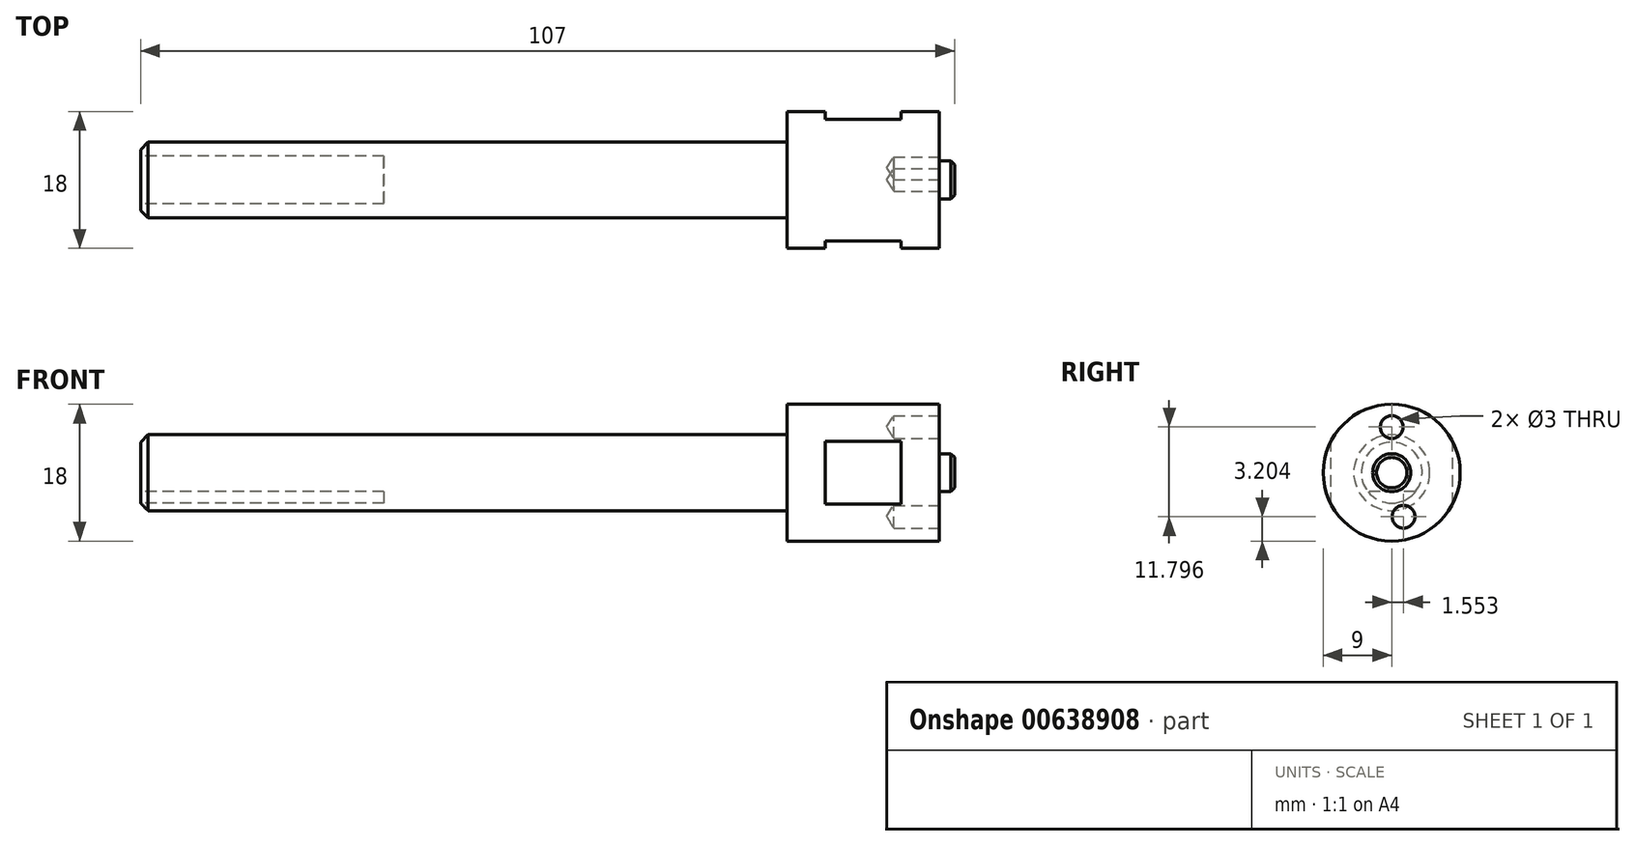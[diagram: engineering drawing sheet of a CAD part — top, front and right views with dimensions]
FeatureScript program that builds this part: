
annotation { "Feature Type Name" : "Feature", "Feature Type Description" : "" }
export const myFeature = defineFeature(function(context is Context, id is Id, definition is map)
    precondition{}
    {
        {
            var Q0;
            Q0=qCreatedBy(makeId("Front.planeOp"),FACE);
            var sketch = newSketch(context, id + "F0", { "sketchPlane" : qUnion([Q0])});
            skCircle(sketch, "E0", {"center": v(-171.85, -5.8) * mm, "radius": 1.23 * mm});
            skArc(sketch, "E1", {"start": v(-171.46, -4.35) * mm, "mid": v(-173.15, -6.55) * mm, "end": v(-170.4, -6.18) * mm});
            skCircle(sketch, "E2", {"center": v(-170.3, 6) * mm, "radius": 1.23 * mm});
            skArc(sketch, "E3", {"start": v(-169.9, 7.45) * mm, "mid": v(-171.6, 5.25) * mm, "end": v(-168.85, 5.61) * mm});
            skLineSegment(sketch, "E4", {"start": v(-162.3, -4.12) * mm, "end": v(-162.3, 4.12) * mm});
            skLineSegment(sketch, "E5", {"start": v(-178.3, -4.12) * mm, "end": v(-178.3, 4.12) * mm});
            skCircle(sketch, "E6", {"center": v(-170.3, 0) * mm, "radius": 9 * mm});
            skLineSegment(sketch, "E7", {"start": v(-174.63, -2.5) * mm, "end": v(-165.97, -2.5) * mm});
            skArc(sketch, "E8", {"start": v(-167.17, -2.5) * mm, "mid": v(-170.3, 4) * mm, "end": v(-173.42, -2.5) * mm});
            skCircle(sketch, "E9", {"center": v(-170.3, 0) * mm, "radius": 2.5 * mm});
            skCircle(sketch, "E10", {"center": v(-170.3, 0) * mm, "radius": 5 * mm});
            skLineSegment(sketch, "E11", {"start": v(1.5, 2.5) * mm, "end": v(1.5, -2.5) * mm});
            skLineSegment(sketch, "E12", {"start": v(2, 0) * mm, "end": v(-108, 0) * mm});
            skLineSegment(sketch, "E13", {"start": v(-104, 5) * mm, "end": v(-20, 5) * mm});
            skLineSegment(sketch, "E14", {"start": v(-73, -5) * mm, "end": v(-20, -5) * mm});
            skLineSegment(sketch, "E15", {"start": v(-105, 4) * mm, "end": v(-104, 5) * mm});
            skLineSegment(sketch, "E16", {"start": v(-105, 4) * mm, "end": v(-105, -2.5) * mm});
            skLineSegment(sketch, "E17", {"start": v(-104, -2.5) * mm, "end": v(-104, 5) * mm});
            skLineSegment(sketch, "E18", {"start": v(-73, -2.5) * mm, "end": v(-73, -5) * mm});
            skLineSegment(sketch, "E19", {"start": v(-105, -2.5) * mm, "end": v(-73, -2.5) * mm});
            skLineSegment(sketch, "E20", {"start": v(2, 2) * mm, "end": v(1.5, 2.5) * mm});
            skLineSegment(sketch, "E21", {"start": v(1.5, -2.5) * mm, "end": v(2, -2) * mm});
            skLineSegment(sketch, "E22", {"start": v(0, 9) * mm, "end": v(0, -9) * mm});
            skLineSegment(sketch, "E23", {"start": v(-9.03, -6) * mm, "end": v(0.82, -6) * mm});
            skLineSegment(sketch, "E24", {"start": v(-6, -7.5) * mm, "end": v(-6.47, -7.23) * mm});
            skLineSegment(sketch, "E25", {"start": v(-6, -4.5) * mm, "end": v(-6.47, -4.77) * mm});
            skLineSegment(sketch, "E26", {"start": v(0, -7.5) * mm, "end": v(-6, -7.5) * mm});
            skLineSegment(sketch, "E27", {"start": v(-6, -4.5) * mm, "end": v(0, -4.5) * mm});
            skLineSegment(sketch, "E28", {"start": v(-6, -7.5) * mm, "end": v(-6, -4.5) * mm});
            skLineSegment(sketch, "E29", {"start": v(-7.5, -7.23) * mm, "end": v(-8.21, -6) * mm});
            skLineSegment(sketch, "E30", {"start": v(-7.5, -4.77) * mm, "end": v(-8.21, -6) * mm});
            skLineSegment(sketch, "E31", {"start": v(-7.5, -4.77) * mm, "end": v(0, -4.77) * mm});
            skLineSegment(sketch, "E32", {"start": v(-7.5, -7.23) * mm, "end": v(-7.5, -4.77) * mm});
            skLineSegment(sketch, "E33", {"start": v(0, -7.23) * mm, "end": v(-7.5, -7.23) * mm});
            skLineSegment(sketch, "E34", {"start": v(-9.03, 6) * mm, "end": v(0.82, 6) * mm});
            skLineSegment(sketch, "E35", {"start": v(-6, 7.5) * mm, "end": v(-6.47, 7.23) * mm});
            skLineSegment(sketch, "E36", {"start": v(-6, 4.5) * mm, "end": v(-6.47, 4.77) * mm});
            skLineSegment(sketch, "E37", {"start": v(0, 7.5) * mm, "end": v(-6, 7.5) * mm});
            skLineSegment(sketch, "E38", {"start": v(-6, 4.5) * mm, "end": v(0, 4.5) * mm});
            skLineSegment(sketch, "E39", {"start": v(-6, 7.5) * mm, "end": v(-6, 4.5) * mm});
            skLineSegment(sketch, "E40", {"start": v(-7.5, 7.23) * mm, "end": v(-8.21, 6) * mm});
            skLineSegment(sketch, "E41", {"start": v(-7.5, 4.77) * mm, "end": v(-8.21, 6) * mm});
            skLineSegment(sketch, "E42", {"start": v(-7.5, 4.77) * mm, "end": v(0, 4.77) * mm});
            skLineSegment(sketch, "E43", {"start": v(-7.5, 7.23) * mm, "end": v(-7.5, 4.77) * mm});
            skLineSegment(sketch, "E44", {"start": v(0, 7.23) * mm, "end": v(-7.5, 7.23) * mm});
            skLineSegment(sketch, "E45", {"start": v(2, 2) * mm, "end": v(2, -2) * mm});
            skLineSegment(sketch, "E46", {"start": v(1.5, 2.5) * mm, "end": v(0, 2.5) * mm});
            skLineSegment(sketch, "E47", {"start": v(-5, -4.12) * mm, "end": v(-15, 4.12) * mm});
            skLineSegment(sketch, "E48", {"start": v(-15, -4.12) * mm, "end": v(-5, 4.12) * mm});
            skLineSegment(sketch, "E49", {"start": v(-5, 4.12) * mm, "end": v(-5, -4.12) * mm});
            skLineSegment(sketch, "E50", {"start": v(-15, 4.12) * mm, "end": v(-15, -4.12) * mm});
            skLineSegment(sketch, "E51", {"start": v(0, -9) * mm, "end": v(-20, -9) * mm});
            skLineSegment(sketch, "E52", {"start": v(-20, 9) * mm, "end": v(-20, -9) * mm});
            skLineSegment(sketch, "E53", {"start": v(0, 9) * mm, "end": v(-20, 9) * mm});
            skLineSegment(sketch, "E54", {"start": v(-5, -4.12) * mm, "end": v(-15, -4.12) * mm});
            skLineSegment(sketch, "E55", {"start": v(-5, 4.12) * mm, "end": v(-15, 4.12) * mm});
            skLineSegment(sketch, "E56", {"start": v(1.5, -2.5) * mm, "end": v(0, -2.5) * mm});
            skLineSegment(sketch, "E57", {"start": v(1.5, 33.8) * mm, "end": v(1.5, 28.8) * mm});
            skLineSegment(sketch, "E58", {"start": v(2, 31.3) * mm, "end": v(-108, 31.3) * mm});
            skLineSegment(sketch, "E59", {"start": v(-104, 36.3) * mm, "end": v(-20, 36.3) * mm});
            skLineSegment(sketch, "E60", {"start": v(-104, 26.3) * mm, "end": v(-20, 26.3) * mm});
            skLineSegment(sketch, "E61", {"start": v(-105, 35.3) * mm, "end": v(-104, 36.3) * mm});
            skLineSegment(sketch, "E62", {"start": v(-105, 35.3) * mm, "end": v(-105, 28.8) * mm});
            skLineSegment(sketch, "E63", {"start": v(-104, 28.8) * mm, "end": v(-104, 36.3) * mm});
            skLineSegment(sketch, "E64", {"start": v(2, 33.3) * mm, "end": v(1.5, 33.8) * mm});
            skLineSegment(sketch, "E65", {"start": v(1.5, 28.8) * mm, "end": v(2, 29.3) * mm});
            skLineSegment(sketch, "E66", {"start": v(0, 40.3) * mm, "end": v(0, 22.3) * mm});
            skLineSegment(sketch, "E67", {"start": v(-9.03, 25.3) * mm, "end": v(0.82, 25.3) * mm});
            skLineSegment(sketch, "E68", {"start": v(-6, 23.8) * mm, "end": v(-6.47, 24.07) * mm});
            skLineSegment(sketch, "E69", {"start": v(-6, 26.8) * mm, "end": v(-6.47, 26.53) * mm});
            skLineSegment(sketch, "E70", {"start": v(0, 23.8) * mm, "end": v(-6, 23.8) * mm});
            skLineSegment(sketch, "E71", {"start": v(-6, 26.8) * mm, "end": v(0, 26.8) * mm});
            skLineSegment(sketch, "E72", {"start": v(-6, 23.8) * mm, "end": v(-6, 26.8) * mm});
            skLineSegment(sketch, "E73", {"start": v(-7.5, 24.07) * mm, "end": v(-8.21, 25.3) * mm});
            skLineSegment(sketch, "E74", {"start": v(-7.5, 26.53) * mm, "end": v(-8.21, 25.3) * mm});
            skLineSegment(sketch, "E75", {"start": v(-7.5, 26.53) * mm, "end": v(0, 26.53) * mm});
            skLineSegment(sketch, "E76", {"start": v(-7.5, 24.07) * mm, "end": v(-7.5, 26.53) * mm});
            skLineSegment(sketch, "E77", {"start": v(0, 24.07) * mm, "end": v(-7.5, 24.07) * mm});
            skLineSegment(sketch, "E78", {"start": v(-9.03, 37.3) * mm, "end": v(0.82, 37.3) * mm});
            skLineSegment(sketch, "E79", {"start": v(-6, 38.8) * mm, "end": v(-6.47, 38.53) * mm});
            skLineSegment(sketch, "E80", {"start": v(-6, 35.8) * mm, "end": v(-6.47, 36.07) * mm});
            skLineSegment(sketch, "E81", {"start": v(0, 38.8) * mm, "end": v(-6, 38.8) * mm});
            skLineSegment(sketch, "E82", {"start": v(-6, 35.8) * mm, "end": v(0, 35.8) * mm});
            skLineSegment(sketch, "E83", {"start": v(-6, 38.8) * mm, "end": v(-6, 35.8) * mm});
            skLineSegment(sketch, "E84", {"start": v(-7.5, 38.53) * mm, "end": v(-8.21, 37.3) * mm});
            skLineSegment(sketch, "E85", {"start": v(-7.5, 36.07) * mm, "end": v(-8.21, 37.3) * mm});
            skLineSegment(sketch, "E86", {"start": v(-7.5, 36.07) * mm, "end": v(0, 36.07) * mm});
            skLineSegment(sketch, "E87", {"start": v(-7.5, 38.53) * mm, "end": v(-7.5, 36.07) * mm});
            skLineSegment(sketch, "E88", {"start": v(0, 38.53) * mm, "end": v(-7.5, 38.53) * mm});
            skLineSegment(sketch, "E89", {"start": v(2, 33.3) * mm, "end": v(2, 29.3) * mm});
            skLineSegment(sketch, "E90", {"start": v(1.5, 33.8) * mm, "end": v(0, 33.8) * mm});
            skLineSegment(sketch, "E91", {"start": v(0, 22.3) * mm, "end": v(-5, 22.3) * mm});
            skLineSegment(sketch, "E92", {"start": v(-20, 40.3) * mm, "end": v(-20, 22.3) * mm});
            skLineSegment(sketch, "E93", {"start": v(0, 40.3) * mm, "end": v(-5, 40.3) * mm});
            skLineSegment(sketch, "E94", {"start": v(1.5, 28.8) * mm, "end": v(0, 28.8) * mm});
            skLineSegment(sketch, "E95", {"start": v(-105, 27.3) * mm, "end": v(-104, 26.3) * mm});
            skLineSegment(sketch, "E96", {"start": v(-105, 27.3) * mm, "end": v(-105, 33.8) * mm});
            skLineSegment(sketch, "E97", {"start": v(-104, 33.8) * mm, "end": v(-104, 26.3) * mm});
            skLineSegment(sketch, "E98", {"start": v(-5, 40.3) * mm, "end": v(-5, 39.3) * mm});
            skLineSegment(sketch, "E99", {"start": v(-15, 40.3) * mm, "end": v(-15, 39.3) * mm});
            skLineSegment(sketch, "E100", {"start": v(-5, 39.3) * mm, "end": v(-15, 39.3) * mm});
            skLineSegment(sketch, "E101", {"start": v(-5, 23.3) * mm, "end": v(-15, 23.3) * mm});
            skLineSegment(sketch, "E102", {"start": v(-5, 23.3) * mm, "end": v(-5, 22.3) * mm});
            skLineSegment(sketch, "E103", {"start": v(-15, 23.3) * mm, "end": v(-15, 22.3) * mm});
            skLineSegment(sketch, "E104", {"start": v(-15, 22.3) * mm, "end": v(-20, 22.3) * mm});
            skLineSegment(sketch, "E105", {"start": v(-15, 40.3) * mm, "end": v(-20, 40.3) * mm});
            skLineSegment(sketch, "E106", {"start": v(-73, 36.3) * mm, "end": v(-73, 26.3) * mm});
            skSolve(sketch);
        }
        {
            var Q0;
            {var subQ0=sQuery(id+"F0.wireOp",EDGE,"E46");Q0=makeQuery(id+"F0.imprint","IMPRINT",FACE,{"disambiguationData":[TD([[makeQuery(id+"F0.imprint","IMPRINT",EDGE,{"derivedFrom":subQ0}),1.0]])]});}
            var Q1;
            {var subQ0=sQuery(id+"F0.wireOp",EDGE,"E49");var subQ1=sQuery(id+"F0.wireOp",EDGE,"E12");var subQ2=makeQuery(id+"F0.imprint","INTERSECT",VERTEX,{"derivedFrom":[subQ1,subQ0]});Q1=makeQuery(id+"F0.imprint","IMPRINT",FACE,{"disambiguationData":[TD([[makeQuery(id+"F0.imprint","IMPRINT",EDGE,{"disambiguationData":[TD([[subQ2,-1.0]])],"derivedFrom":subQ1}),-1.0]])]});}
            var Q2;
            {var subQ0=sQuery(id+"F0.wireOp",EDGE,"E40");Q2=makeQuery(id+"F0.imprint","IMPRINT",FACE,{"disambiguationData":[TD([[makeQuery(id+"F0.imprint","IMPRINT",EDGE,{"derivedFrom":subQ0}),1.0]])]});}
            var Q3;
            {var subQ0=sQuery(id+"F0.wireOp",EDGE,"E50");var subQ1=sQuery(id+"F0.wireOp",EDGE,"E12");var subQ2=makeQuery(id+"F0.imprint","INTERSECT",VERTEX,{"derivedFrom":[subQ1,subQ0]});Q3=makeQuery(id+"F0.imprint","IMPRINT",FACE,{"disambiguationData":[TD([[makeQuery(id+"F0.imprint","IMPRINT",EDGE,{"disambiguationData":[TD([[subQ2,1.0]])],"derivedFrom":subQ1}),-1.0]])]});}
            var Q4;
            {var subQ5=sQuery(id+"F0.wireOp",EDGE,"E13");Q4=makeQuery(id+"F0.imprint","IMPRINT",FACE,{"disambiguationData":[TD([[makeQuery(id+"F0.imprint","IMPRINT",EDGE,{"derivedFrom":subQ5}),-1.0]])]});}
            var Q5;
            {var subQ17=sQuery(id+"F0.wireOp",EDGE,"E35");Q5=makeQuery(id+"F0.imprint","IMPRINT",FACE,{"disambiguationData":[TD([[makeQuery(id+"F0.imprint","IMPRINT",EDGE,{"derivedFrom":subQ17}),-1.0]])]});}
            var Q6;
            {var subQ0=sQuery(id+"F0.wireOp",EDGE,"E55");Q6=makeQuery(id+"F0.imprint","IMPRINT",FACE,{"disambiguationData":[TD([[makeQuery(id+"F0.imprint","IMPRINT",EDGE,{"derivedFrom":subQ0}),1.0]])]});}
            var Q7;
            {var subQ0=sQuery(id+"F0.wireOp",EDGE,"E44");var subQ1=sQuery(id+"F0.wireOp",EDGE,"E22");var subQ2=makeQuery(id+"F0.imprint","INTERSECT",VERTEX,{"derivedFrom":[subQ1,subQ0]});Q7=makeQuery(id+"F0.imprint","IMPRINT",FACE,{"disambiguationData":[TD([[makeQuery(id+"F0.imprint","IMPRINT",EDGE,{"disambiguationData":[TD([[subQ2,-1.0]])],"derivedFrom":subQ1}),-1.0]])]});}
            var Q8;
            {var subQ0=sQuery(id+"F0.wireOp",EDGE,"E20");Q8=makeQuery(id+"F0.imprint","IMPRINT",FACE,{"disambiguationData":[TD([[makeQuery(id+"F0.imprint","IMPRINT",EDGE,{"derivedFrom":subQ0}),1.0]])]});}
            var Q9;
            {var subQ0=sQuery(id+"F0.wireOp",EDGE,"E42");var subQ1=sQuery(id+"F0.wireOp",EDGE,"E22");var subQ2=makeQuery(id+"F0.imprint","INTERSECT",VERTEX,{"derivedFrom":[subQ1,subQ0]});Q9=makeQuery(id+"F0.imprint","IMPRINT",FACE,{"disambiguationData":[TD([[makeQuery(id+"F0.imprint","IMPRINT",EDGE,{"disambiguationData":[TD([[subQ2,1.0]])],"derivedFrom":subQ1}),-1.0]])]});}
            var Q10;
            {var subQ4=sQuery(id+"F0.wireOp",EDGE,"E34");var subQ6=sQuery(id+"F0.wireOp",EDGE,"E43");var subQ8=makeQuery(id+"F0.imprint","INTERSECT",VERTEX,{"derivedFrom":[subQ4,subQ6]});Q10=makeQuery(id+"F0.imprint","IMPRINT",FACE,{"disambiguationData":[TD([[makeQuery(id+"F0.imprint","IMPRINT",EDGE,{"disambiguationData":[TD([[subQ8,-1.0]])],"derivedFrom":subQ4}),1.0]])]});}
            var Q11;
            {var subQ2=sQuery(id+"F0.wireOp",EDGE,"E43");var subQ6=sQuery(id+"F0.wireOp",EDGE,"E34");var subQ8=makeQuery(id+"F0.imprint","INTERSECT",VERTEX,{"derivedFrom":[subQ6,subQ2]});Q11=makeQuery(id+"F0.imprint","IMPRINT",FACE,{"disambiguationData":[TD([[makeQuery(id+"F0.imprint","IMPRINT",EDGE,{"disambiguationData":[TD([[subQ8,-1.0]])],"derivedFrom":subQ6}),-1.0]])]});}
            var Q12;
            {var subQ0=sQuery(id+"F0.wireOp",EDGE,"E41");Q12=makeQuery(id+"F0.imprint","IMPRINT",FACE,{"disambiguationData":[TD([[makeQuery(id+"F0.imprint","IMPRINT",EDGE,{"derivedFrom":subQ0}),-1.0]])]});}
            var Q13;
            {var subQ0=sQuery(id+"F0.wireOp",EDGE,"E37");Q13=makeQuery(id+"F0.imprint","IMPRINT",FACE,{"disambiguationData":[TD([[makeQuery(id+"F0.imprint","IMPRINT",EDGE,{"derivedFrom":subQ0}),1.0]])]});}
            var Q14;
            {var subQ0=sQuery(id+"F0.wireOp",EDGE,"E38");Q14=makeQuery(id+"F0.imprint","IMPRINT",FACE,{"disambiguationData":[TD([[makeQuery(id+"F0.imprint","IMPRINT",EDGE,{"derivedFrom":subQ0}),1.0]])]});}
            var Q15;
            {var subQ0=sQuery(id+"F0.wireOp",EDGE,"E36");Q15=makeQuery(id+"F0.imprint","IMPRINT",FACE,{"disambiguationData":[TD([[makeQuery(id+"F0.imprint","IMPRINT",EDGE,{"derivedFrom":subQ0}),-1.0]])]});}
            var Q16;
            {var subQ0=sQuery(id+"F0.wireOp",EDGE,"E35");Q16=makeQuery(id+"F0.imprint","IMPRINT",FACE,{"disambiguationData":[TD([[makeQuery(id+"F0.imprint","IMPRINT",EDGE,{"derivedFrom":subQ0}),1.0]])]});}
            var Q17;
            {var subQ5=sQuery(id+"F0.wireOp",EDGE,"E15");Q17=makeQuery(id+"F0.imprint","IMPRINT",FACE,{"disambiguationData":[TD([[makeQuery(id+"F0.imprint","IMPRINT",EDGE,{"derivedFrom":subQ5}),-1.0]])]});}
            var Q18;
            Q18=sQuery(id+"F0.wireOp",EDGE,"E12");
            revolve(context, id + "F1", {"entities" : qUnion([Q0, Q1, Q2, Q3, Q4, Q5, Q6, Q7, Q8, Q9, Q10, Q11, Q12, Q13, Q14, Q15, Q16, Q17]), "axis" : qUnion([Q18]), "revolveType" : RevolveType.FULL});
        }
        {
            var Q0;
            Q0=makeQuery(id+"F1.opRevolve","SWEPT_FACE",FACE,{"disambiguationData":[OSD([sQuery(id+"F0.wireOp",EDGE,"E16")])]});
            var sketch = newSketch(context, id + "F2", { "sketchPlane" : qUnion([Q0])});
            skCircle(sketch, "E107.0", {"center": v(0, 0) * mm, "radius": 5 * mm});
            skLineSegment(sketch, "E108.0", {"start": v(-4.33, -2.5) * mm, "end": v(4.33, -2.5) * mm});
            skCircle(sketch, "E109.0", {"center": v(0, 0) * mm, "radius": 4 * mm});
            skSolve(sketch);
        }
        {
            var Q0;
            {var subQ0=sQuery(id+"F2.wireOp",EDGE,"E108.0");var subQ1=makeQuery(id+"F1.opRevolve","SWEPT_EDGE",EDGE,{"disambiguationData":[OSD([sQuery(id+"F0.wireOp",EDGE,"E15"),sQuery(id+"F0.wireOp",EDGE,"E16")])]});var subQ2=makeQuery(id+"F2.imprint","INTERSECT",VERTEX,{"disambiguationData":[OD(0.0)],"derivedFrom":[subQ1,subQ0]});Q0=makeQuery(id+"F2.imprint","IMPRINT",FACE,{"disambiguationData":[TD([[makeQuery(id+"F2.imprint","IMPRINT",EDGE,{"disambiguationData":[TD([[subQ2,-1.0]])],"derivedFrom":subQ0}),-1.0]])]});}
            var Q1;
            {var subQ0=sQuery(id+"F2.wireOp",EDGE,"E108.0");var subQ1=sQuery(id+"F2.wireOp",EDGE,"E107.0");var subQ2=makeQuery(id+"F2.imprint","INTERSECT",VERTEX,{"disambiguationData":[OD(0.0)],"derivedFrom":[subQ1,subQ0]});Q1=makeQuery(id+"F2.imprint","IMPRINT",FACE,{"disambiguationData":[TD([[makeQuery(id+"F2.imprint","IMPRINT",EDGE,{"disambiguationData":[TD([[subQ2,1.0]])],"derivedFrom":subQ1}),-1.0]])]});}
            var Q2;
            {var subQ0=sQuery(id+"F2.wireOp",EDGE,"E109.0");var subQ1=sQuery(id+"F2.wireOp",EDGE,"E108.0");var subQ2=makeQuery(id+"F2.imprint","INTERSECT",VERTEX,{"disambiguationData":[OD(0.0)],"derivedFrom":[subQ1,subQ0]});Q2=makeQuery(id+"F2.imprint","IMPRINT",FACE,{"disambiguationData":[TD([[makeQuery(id+"F2.imprint","IMPRINT",EDGE,{"disambiguationData":[TD([[subQ2,-1.0]])],"derivedFrom":subQ1}),-1.0]])]});}
            extrude(context, id + "F3", {"entities" : qUnion([Q0, Q1, Q2]), "operationType" : NewBodyOperationType.REMOVE, "oppositeDirection" : true, "depth" : 32 * mm, "offsetDistance" : 25 * mm});
        }
        {
            var Q0;
            Q0=qCreatedBy(makeId("Top.planeOp"),FACE);
            var sketch = newSketch(context, id + "F4", { "sketchPlane" : qUnion([Q0])});
            skLineSegment(sketch, "E110", {"start": v(1.5, 2.5) * mm, "end": v(1.5, -2.5) * mm});
            skLineSegment(sketch, "E111", {"start": v(2, 0) * mm, "end": v(-108, 0) * mm});
            skLineSegment(sketch, "E112", {"start": v(-104, 5) * mm, "end": v(-20, 5) * mm});
            skLineSegment(sketch, "E113", {"start": v(-104, -5) * mm, "end": v(-20, -5) * mm});
            skLineSegment(sketch, "E114", {"start": v(-105, 4) * mm, "end": v(-104, 5) * mm});
            skLineSegment(sketch, "E115", {"start": v(-105, 4) * mm, "end": v(-105, -2.5) * mm});
            skLineSegment(sketch, "E116", {"start": v(-104, -2.5) * mm, "end": v(-104, 5) * mm});
            skLineSegment(sketch, "E117", {"start": v(2, 2) * mm, "end": v(1.5, 2.5) * mm});
            skLineSegment(sketch, "E118", {"start": v(1.5, -2.5) * mm, "end": v(2, -2) * mm});
            skLineSegment(sketch, "E119", {"start": v(0, 9) * mm, "end": v(0, -9) * mm});
            skLineSegment(sketch, "E120", {"start": v(-9.03, -6) * mm, "end": v(0.82, -6) * mm});
            skLineSegment(sketch, "E121", {"start": v(-6, -7.5) * mm, "end": v(-6.47, -7.23) * mm});
            skLineSegment(sketch, "E122", {"start": v(-6, -4.5) * mm, "end": v(-6.47, -4.77) * mm});
            skLineSegment(sketch, "E123", {"start": v(0, -7.5) * mm, "end": v(-6, -7.5) * mm});
            skLineSegment(sketch, "E124", {"start": v(-6, -4.5) * mm, "end": v(0, -4.5) * mm});
            skLineSegment(sketch, "E125", {"start": v(-6, -7.5) * mm, "end": v(-6, -4.5) * mm});
            skLineSegment(sketch, "E126", {"start": v(-7.5, -7.23) * mm, "end": v(-8.21, -6) * mm});
            skLineSegment(sketch, "E127", {"start": v(-7.5, -4.77) * mm, "end": v(-8.21, -6) * mm});
            skLineSegment(sketch, "E128", {"start": v(-7.5, -4.77) * mm, "end": v(0, -4.77) * mm});
            skLineSegment(sketch, "E129", {"start": v(-7.5, -7.23) * mm, "end": v(-7.5, -4.77) * mm});
            skLineSegment(sketch, "E130", {"start": v(0, -7.23) * mm, "end": v(-7.5, -7.23) * mm});
            skLineSegment(sketch, "E131", {"start": v(-9.03, 6) * mm, "end": v(0.82, 6) * mm});
            skLineSegment(sketch, "E132", {"start": v(-6, 7.5) * mm, "end": v(-6.47, 7.23) * mm});
            skLineSegment(sketch, "E133", {"start": v(-6, 4.5) * mm, "end": v(-6.47, 4.77) * mm});
            skLineSegment(sketch, "E134", {"start": v(0, 7.5) * mm, "end": v(-6, 7.5) * mm});
            skLineSegment(sketch, "E135", {"start": v(-6, 4.5) * mm, "end": v(0, 4.5) * mm});
            skLineSegment(sketch, "E136", {"start": v(-6, 7.5) * mm, "end": v(-6, 4.5) * mm});
            skLineSegment(sketch, "E137", {"start": v(-7.5, 7.23) * mm, "end": v(-8.21, 6) * mm});
            skLineSegment(sketch, "E138", {"start": v(-7.5, 4.77) * mm, "end": v(-8.21, 6) * mm});
            skLineSegment(sketch, "E139", {"start": v(-7.5, 4.77) * mm, "end": v(0, 4.77) * mm});
            skLineSegment(sketch, "E140", {"start": v(-7.5, 7.23) * mm, "end": v(-7.5, 4.77) * mm});
            skLineSegment(sketch, "E141", {"start": v(0, 7.23) * mm, "end": v(-7.5, 7.23) * mm});
            skLineSegment(sketch, "E142", {"start": v(2, 2) * mm, "end": v(2, -2) * mm});
            skLineSegment(sketch, "E143", {"start": v(1.5, 2.5) * mm, "end": v(0, 2.5) * mm});
            skLineSegment(sketch, "E144", {"start": v(0, -9) * mm, "end": v(-5, -9) * mm});
            skLineSegment(sketch, "E145", {"start": v(-20, 9) * mm, "end": v(-20, -9) * mm});
            skLineSegment(sketch, "E146", {"start": v(0, 9) * mm, "end": v(-5, 9) * mm});
            skLineSegment(sketch, "E147", {"start": v(1.5, -2.5) * mm, "end": v(0, -2.5) * mm});
            skLineSegment(sketch, "E148", {"start": v(-105, -4) * mm, "end": v(-104, -5) * mm});
            skLineSegment(sketch, "E149", {"start": v(-105, -4) * mm, "end": v(-105, 2.5) * mm});
            skLineSegment(sketch, "E150", {"start": v(-104, 2.5) * mm, "end": v(-104, -5) * mm});
            skLineSegment(sketch, "E151", {"start": v(-5, 9) * mm, "end": v(-5, 8) * mm});
            skLineSegment(sketch, "E152", {"start": v(-15, 9) * mm, "end": v(-15, 8) * mm});
            skLineSegment(sketch, "E153", {"start": v(-5, 8) * mm, "end": v(-15, 8) * mm});
            skLineSegment(sketch, "E154", {"start": v(-5, -8) * mm, "end": v(-15, -8) * mm});
            skLineSegment(sketch, "E155", {"start": v(-5, -8) * mm, "end": v(-5, -9) * mm});
            skLineSegment(sketch, "E156", {"start": v(-15, -8) * mm, "end": v(-15, -9) * mm});
            skLineSegment(sketch, "E157", {"start": v(-15, -9) * mm, "end": v(-20, -9) * mm});
            skLineSegment(sketch, "E158", {"start": v(-15, 9) * mm, "end": v(-20, 9) * mm});
            skLineSegment(sketch, "E159", {"start": v(-73, 5) * mm, "end": v(-73, -5) * mm});
            skLineSegment(sketch, "E160", {"start": v(-20, 9) * mm, "end": v(0, 9) * mm});
            skLineSegment(sketch, "E161", {"start": v(0, -9) * mm, "end": v(-20, -9) * mm});
            skSolve(sketch);
        }
        {
            var Q0;
            Q0=makeQuery(id+"F4.imprint","IMPRINT",FACE,{"disambiguationData":[TD([[makeQuery(id+"F4.imprint","IMPRINT",EDGE,{"derivedFrom":sQuery(id+"F4.wireOp",EDGE,"E154")}),1.0]])]});
            var Q1;
            {var subQ0=sQuery(id+"F4.wireOp",EDGE,"E151");Q1=makeQuery(id+"F4.imprint","IMPRINT",FACE,{"disambiguationData":[TD([[makeQuery(id+"F4.imprint","IMPRINT",EDGE,{"derivedFrom":subQ0}),-1.0]])]});}
            extrude(context, id + "F5", {"entities" : qUnion([Q0, Q1]), "operationType" : NewBodyOperationType.REMOVE, "endBound" : BoundingType.SYMMETRIC, "oppositeDirection" : true, "depth" : 25 * mm, "offsetDistance" : 25 * mm});
        }
        {
            var Q0;
            Q0=makeQuery(id+"F1.opRevolve","SWEPT_FACE",FACE,{"disambiguationData":[OSD([sQuery(id+"F0.wireOp",EDGE,"E52")])]});
            var sketch = newSketch(context, id + "F6", { "sketchPlane" : qUnion([Q0])});
            skCircle(sketch, "E162", {"center": v(-1.55, -5.8) * mm, "radius": 1.23 * mm});
            skArc(sketch, "E163", {"start": v(-1.16, -4.35) * mm, "mid": v(-2.85, -6.55) * mm, "end": v(-0.1, -6.18) * mm});
            skCircle(sketch, "E164", {"center": v(0, 6) * mm, "radius": 1.23 * mm});
            skArc(sketch, "E165", {"start": v(0.39, 7.45) * mm, "mid": v(-1.3, 5.25) * mm, "end": v(1.45, 5.61) * mm});
            skLineSegment(sketch, "E166", {"start": v(8, -4.12) * mm, "end": v(8, 4.12) * mm});
            skLineSegment(sketch, "E167", {"start": v(-8, -4.12) * mm, "end": v(-8, 4.12) * mm});
            skCircle(sketch, "E168", {"center": v(0, 0) * mm, "radius": 9 * mm});
            skLineSegment(sketch, "E169", {"start": v(-4.33, -2.5) * mm, "end": v(4.33, -2.5) * mm});
            skArc(sketch, "E170", {"start": v(3.12, -2.5) * mm, "mid": v(0, 4) * mm, "end": v(-3.12, -2.5) * mm});
            skCircle(sketch, "E171", {"center": v(0, 0) * mm, "radius": 2.5 * mm});
            skCircle(sketch, "E172", {"center": v(0, 0) * mm, "radius": 5 * mm});
            skSolve(sketch);
        }
        {
            var Q0;
            Q0=makeQuery(id+"F1.opRevolve","SWEPT_FACE",FACE,{"disambiguationData":[OSD([sQuery(id+"F0.wireOp",EDGE,"E22")])]});
            var sketch = newSketch(context, id + "F7", { "sketchPlane" : qUnion([Q0])});
            skPoint(sketch, "E173.0", {"position": v(0, 6) * mm});
            skPoint(sketch, "E174.0", {"position": v(1.55, -5.8) * mm});
            skSolve(sketch);
        }
        {
            var Q0;
            Q0=sQuery(id+"F7.wireOp",VERTEX,"E173.0");
            var Q1;
            Q1=sQuery(id+"F7.wireOp",VERTEX,"E174.0");
            var Q2;
            Q2=makeQuery(id+"F1.opRevolve","SWEPT_BODY",BODY,{"disambiguationData":[OSD([sQuery(id+"F0.wireOp",EDGE,"E12"),sQuery(id+"F0.wireOp",EDGE,"E13"),sQuery(id+"F0.wireOp",EDGE,"E15"),sQuery(id+"F0.wireOp",EDGE,"E16"),sQuery(id+"F0.wireOp",EDGE,"E20"),sQuery(id+"F0.wireOp",EDGE,"E22"),sQuery(id+"F0.wireOp",EDGE,"E45"),sQuery(id+"F0.wireOp",EDGE,"E46"),sQuery(id+"F0.wireOp",EDGE,"E52"),sQuery(id+"F0.wireOp",EDGE,"E53")])]});
            hole(context, id + "F8", {"style" : HoleStyle.SIMPLE, "endStyle" : HoleEndStyle.BLIND, "holeDiameter" : 3 * mm, "majorDiameter" : 5 * mm, "holeDepth" : 6 * mm, "isTappedThrough" : true, "tappedDepth" : 12 * mm, "tapClearance" : 3, "locations" : qUnion([Q0, Q1]), "scope" : qUnion([Q2])});
        }
    });
